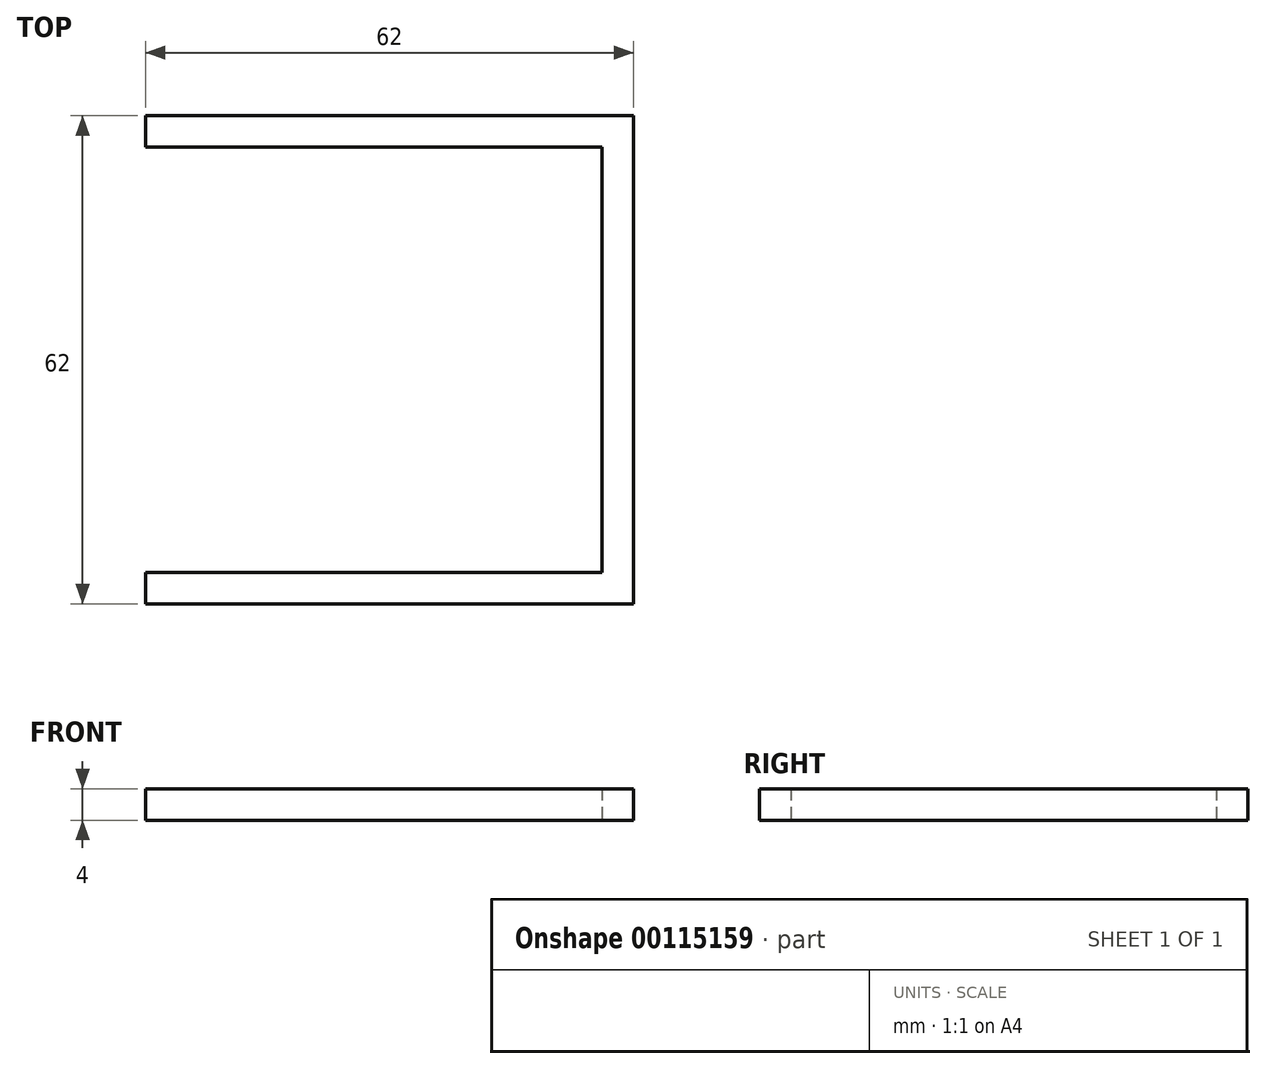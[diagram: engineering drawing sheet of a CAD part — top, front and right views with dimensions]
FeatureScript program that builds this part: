
annotation { "Feature Type Name" : "Feature", "Feature Type Description" : "" }
export const myFeature = defineFeature(function(context is Context, id is Id, definition is map)
    precondition{}
    {
        {
            var Q0;
            Q0=qCreatedBy(makeId("Top.planeOp"),FACE);
            var sketch = newSketch(context, id + "F0", { "sketchPlane" : qUnion([Q0])});
            skLineSegment(sketch, "E0.bottom", {"start": v(26.25, 26.25) * mm, "end": v(-26.25, 26.25) * mm, "construction": true});
            skLineSegment(sketch, "E0.top", {"start": v(26.25, -26.25) * mm, "end": v(-26.25, -26.25) * mm, "construction": true});
            skLineSegment(sketch, "E0.left", {"start": v(26.25, 26.25) * mm, "end": v(26.25, -26.25) * mm, "construction": true});
            skLineSegment(sketch, "E0.right", {"start": v(-26.25, 26.25) * mm, "end": v(-26.25, -26.25) * mm, "construction": true});
            skPoint(sketch, "E0.middle", {"position": v(0, 0) * mm});
            skLineSegment(sketch, "E1.bottom", {"start": v(31, 31) * mm, "end": v(-31, 31) * mm});
            skLineSegment(sketch, "E1.top", {"start": v(31, -31) * mm, "end": v(-31, -31) * mm});
            skLineSegment(sketch, "E1.left", {"start": v(31, 31) * mm, "end": v(31, -31) * mm});
            skLineSegment(sketch, "E1.right", {"start": v(-31, 31) * mm, "end": v(-31, -31) * mm, "construction": true});
            skLineSegment(sketch, "E2.bottom", {"start": v(27, 27) * mm, "end": v(-27, 27) * mm});
            skLineSegment(sketch, "E2.top", {"start": v(27, -27) * mm, "end": v(-27, -27) * mm});
            skLineSegment(sketch, "E2.left", {"start": v(27, 27) * mm, "end": v(27, -27) * mm});
            skLineSegment(sketch, "E2.right", {"start": v(-27, 27) * mm, "end": v(-27, -27) * mm, "construction": true});
            skLineSegment(sketch, "E3", {"start": v(-27, 27) * mm, "end": v(-31, 27) * mm});
            skLineSegment(sketch, "E4", {"start": v(-31, 27) * mm, "end": v(-31, 31) * mm});
            skLineSegment(sketch, "E5", {"start": v(-27, -27) * mm, "end": v(-31, -27) * mm});
            skLineSegment(sketch, "E6", {"start": v(-31, -27) * mm, "end": v(-31, -31) * mm});
            skSolve(sketch);
        }
        {
            var Q0;
            Q0=makeQuery(id+"F0.imprint","IMPRINT",FACE,{"disambiguationData":[TD([[makeQuery(id+"F0.imprint","IMPRINT",EDGE,{"derivedFrom":sQuery(id+"F0.wireOp",EDGE,"E1.bottom")}),1.0]])]});
            extrude(context, id + "F1", {"entities" : qUnion([Q0]), "depth" : 4 * mm});
        }
    });
